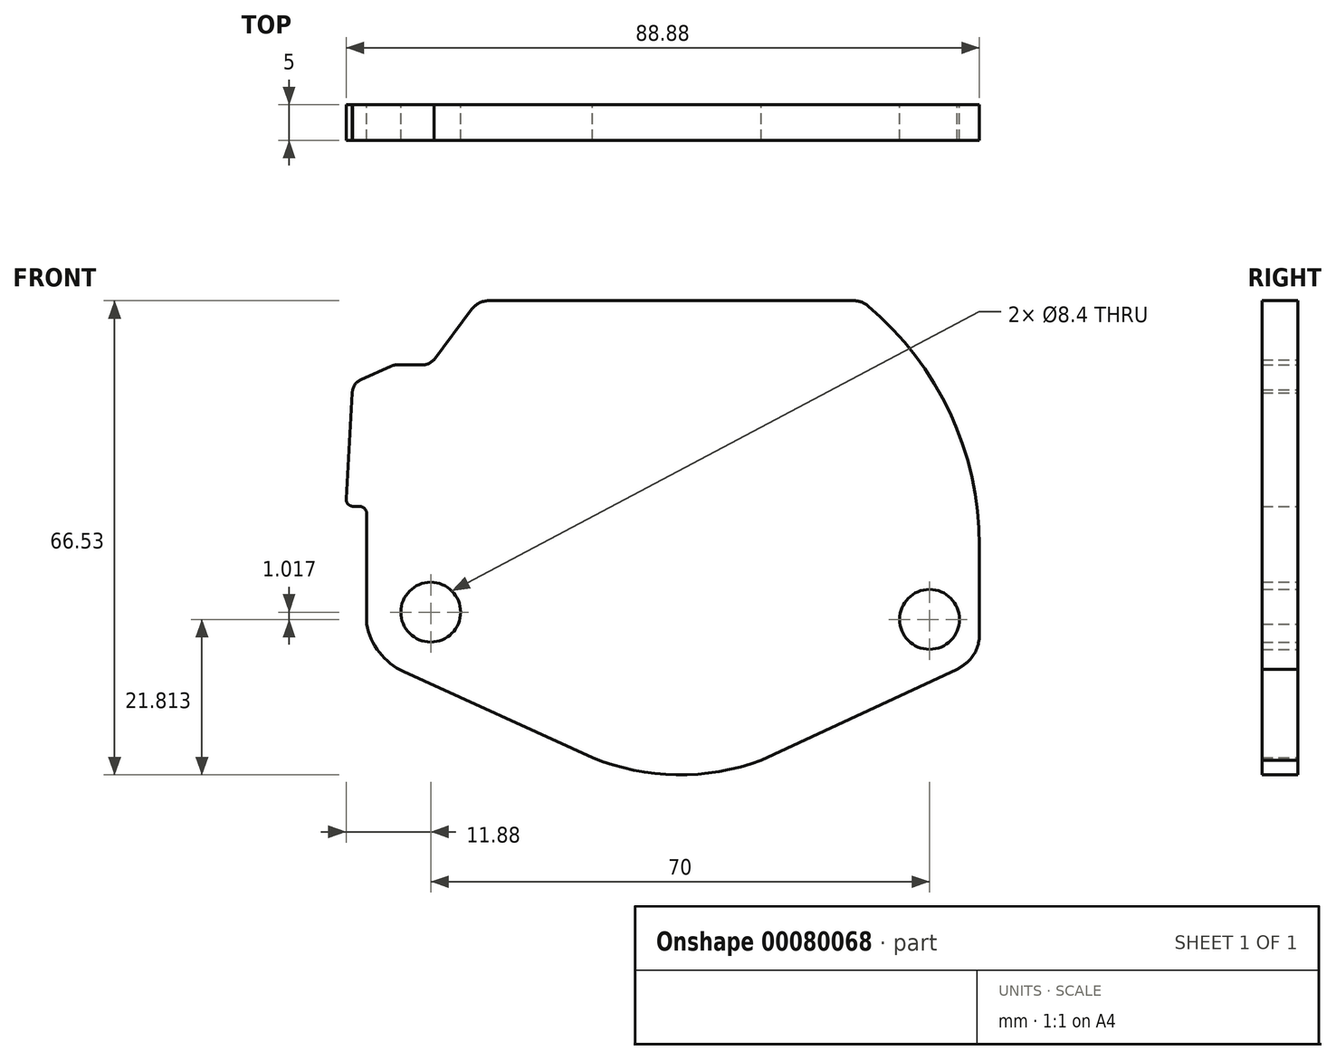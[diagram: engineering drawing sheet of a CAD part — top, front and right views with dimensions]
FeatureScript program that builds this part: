
annotation { "Feature Type Name" : "Feature", "Feature Type Description" : "" }
export const myFeature = defineFeature(function(context is Context, id is Id, definition is map)
    precondition{}
    {
        {
            var Q0;
            Q0=qCreatedBy(makeId("Front.planeOp"),FACE);
            var sketch = newSketch(context, id + "F0", { "sketchPlane" : qUnion([Q0])});
            skLineSegment(sketch, "E0.bottom", {"start": v(-20.82, 33.91) * mm, "end": v(21.5, 33.91) * mm});
            skPoint(sketch, "E1", {"position": v(0, 0) * mm});
            skCircle(sketch, "E2", {"center": v(-35, -9.79) * mm, "radius": 4.2 * mm});
            skCircle(sketch, "E3.MirrorC", {"center": v(35, -10.8) * mm, "radius": 4.2 * mm});
            skArc(sketch, "E4", {"start": v(-14.74, -29.1) * mm, "mid": v(-1.85, -32.57) * mm, "end": v(11.35, -30.59) * mm});
            skArc(sketch, "E5", {"start": v(38.9, -17.8) * mm, "mid": v(39.64, -17.32) * mm, "end": v(40.33, -16.77) * mm});
            skLineSegment(sketch, "E6", {"start": v(38.9, -17.8) * mm, "end": v(11.35, -30.59) * mm});
            skLineSegment(sketch, "E7", {"start": v(42, -0.42) * mm, "end": v(42, -13.04) * mm});
            skArc(sketch, "E8", {"start": v(-44, -11.48) * mm, "mid": v(-42.21, -15.43) * mm, "end": v(-38.8, -18.12) * mm});
            skLineSegment(sketch, "E9", {"start": v(-12.34, -30.2) * mm, "end": v(-38.8, -18.12) * mm});
            skLineSegment(sketch, "E10", {"start": v(-44, -11.48) * mm, "end": v(-44, 4.06) * mm});
            skPoint(sketch, "E11.visualSharp", {"position": v(24.25, 33.91) * mm});
            skLineSegment(sketch, "E12", {"start": v(-39.77, 24.91) * mm, "end": v(-36.12, 24.91) * mm});
            skLineSegment(sketch, "E13", {"start": v(-20.82, 33.91) * mm, "end": v(-22.32, 33.91) * mm});
            skPoint(sketch, "E14.visualSharp", {"position": v(-25.07, 33.91) * mm});
            skArc(sketch, "E15.filletArc", {"start": v(-36.12, 24.91) * mm, "mid": v(-35.26, 25.1) * mm, "end": v(-34.57, 25.65) * mm});
            skPoint(sketch, "E16.visualSharp", {"position": v(42, -14.68) * mm});
            skArc(sketch, "E16.filletArc", {"start": v(40.33, -16.77) * mm, "mid": v(41.56, -15.08) * mm, "end": v(42, -13.04) * mm});
            skLineSegment(sketch, "E17", {"start": v(21.5, 33.91) * mm, "end": v(24.42, 33.91) * mm});
            skArc(sketch, "E18", {"start": v(42, -0.42) * mm, "mid": v(37.9, 18.12) * mm, "end": v(26.36, 33.2) * mm});
            skPoint(sketch, "E19.visualSharp", {"position": v(25.5, 33.91) * mm});
            skArc(sketch, "E19.filletArc", {"start": v(26.36, 33.2) * mm, "mid": v(25.45, 33.73) * mm, "end": v(24.42, 33.91) * mm});
            skLineSegment(sketch, "E20", {"start": v(-22.32, 33.91) * mm, "end": v(-26.86, 33.91) * mm});
            skLineSegment(sketch, "E21", {"start": v(-34.57, 25.65) * mm, "end": v(-29.25, 32.71) * mm});
            skPoint(sketch, "E22.visualSharp", {"position": v(-28.35, 33.91) * mm});
            skArc(sketch, "E22.filletArc", {"start": v(-26.86, 33.91) * mm, "mid": v(-28.2, 33.6) * mm, "end": v(-29.25, 32.71) * mm});
            skLineSegment(sketch, "E23", {"start": v(-45, 5.06) * mm, "end": v(-45.88, 5.06) * mm});
            skArc(sketch, "E24", {"start": v(-44.82, 22.82) * mm, "mid": v(-45.56, 22.26) * mm, "end": v(-45.96, 21.42) * mm});
            skLineSegment(sketch, "E25", {"start": v(-46.88, 6.12) * mm, "end": v(-46, 21) * mm});
            skLineSegment(sketch, "E26", {"start": v(-40.59, 24.73) * mm, "end": v(-44.82, 22.82) * mm});
            skLineSegment(sketch, "E27", {"start": v(-45.96, 21.42) * mm, "end": v(-46, 21) * mm});
            skPoint(sketch, "E28.visualSharp", {"position": v(-40.2, 24.91) * mm});
            skArc(sketch, "E28.filletArc", {"start": v(-39.77, 24.91) * mm, "mid": v(-40.19, 24.87) * mm, "end": v(-40.59, 24.73) * mm});
            skPoint(sketch, "E29.visualSharp", {"position": v(-46.94, 5.06) * mm});
            skArc(sketch, "E29.filletArc", {"start": v(-46.88, 6.12) * mm, "mid": v(-46.6, 5.37) * mm, "end": v(-45.88, 5.06) * mm});
            skPoint(sketch, "E30.visualSharp", {"position": v(-44, 5.06) * mm});
            skArc(sketch, "E30.filletArc", {"start": v(-44, 4.06) * mm, "mid": v(-44.3, 4.77) * mm, "end": v(-45, 5.06) * mm});
            skSolve(sketch);
        }
        {
            var Q0;
            Q0=makeQuery(id+"F0.imprint","IMPRINT",FACE,{"disambiguationData":[TD([[makeQuery(id+"F0.imprint","IMPRINT",EDGE,{"derivedFrom":sQuery(id+"F0.wireOp",EDGE,"E0.bottom")}),-1.0]])]});
            extrude(context, id + "F1", {"entities" : qUnion([Q0]), "depth" : 5 * mm});
        }
    });
